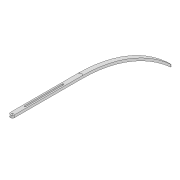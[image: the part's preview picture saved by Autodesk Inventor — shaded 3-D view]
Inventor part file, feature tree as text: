
AUTODESK INVENTOR PART (.ipt)
format: ipt  version: 2022 (Build 260153000, 153)  size: 122,368 bytes
history: native  units: mm
features: extrude x2, sketch x2, projected_geometry x2, fillet x1
ambient origin geometry x8: Origin, YZ Plane, XZ Plane, XY Plane, X Axis, Y Axis, Z Axis, Center Point
bodies: Solid1 (feature_tree)
feature tree (7):
  extrude  "Extrusion1"  Depth=10.0mm
  extrude  "Extrusion2"  Depth=2.0mm
  fillet  "Fillet1"  Radius=120.0mm
  sketch  "Sketch1"  dims[d0=160.0mm d1=10.0mm]
  sketch  "Sketch2"  dims[d2=3.3mm d3=30.0mm d5=120.0mm d6=3.3mm d7=6.0mm d8=0.0mm d9=6.0mm d10=373.775mm d11=90.0mm d12=10.0mm d13=0.0mm d14=2.0mm]
  projected_geometry  "Projected Loop1"
  projected_geometry  "Projected Loop2"
